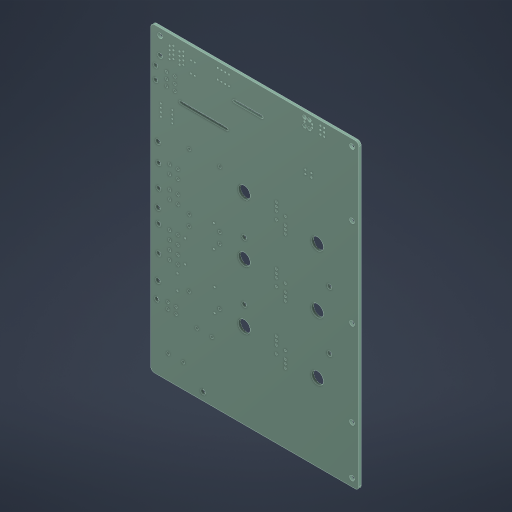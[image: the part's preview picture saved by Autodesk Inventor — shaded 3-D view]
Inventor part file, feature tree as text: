
AUTODESK INVENTOR PART (.ipt)
format: ipt  version: 2024.2 (Build 282272000, 272)  size: 457,728 bytes
history: native  units: in
note: dims shown in document units (in); Inventor stores cm internally (conversion verified against a paired STEP export)
features: sketch x1, projected_geometry x1, imported_body x1
ambient origin geometry x8: Origin, YZ Plane, XZ Plane, XY Plane, X Axis, Y Axis, Z Axis, Center Point
bodies: Solid1 (feature_tree)
feature tree (3):
  sketch  "Sketch1"
  projected_geometry  "Projected Loop1"
  imported_body  "Base1"
